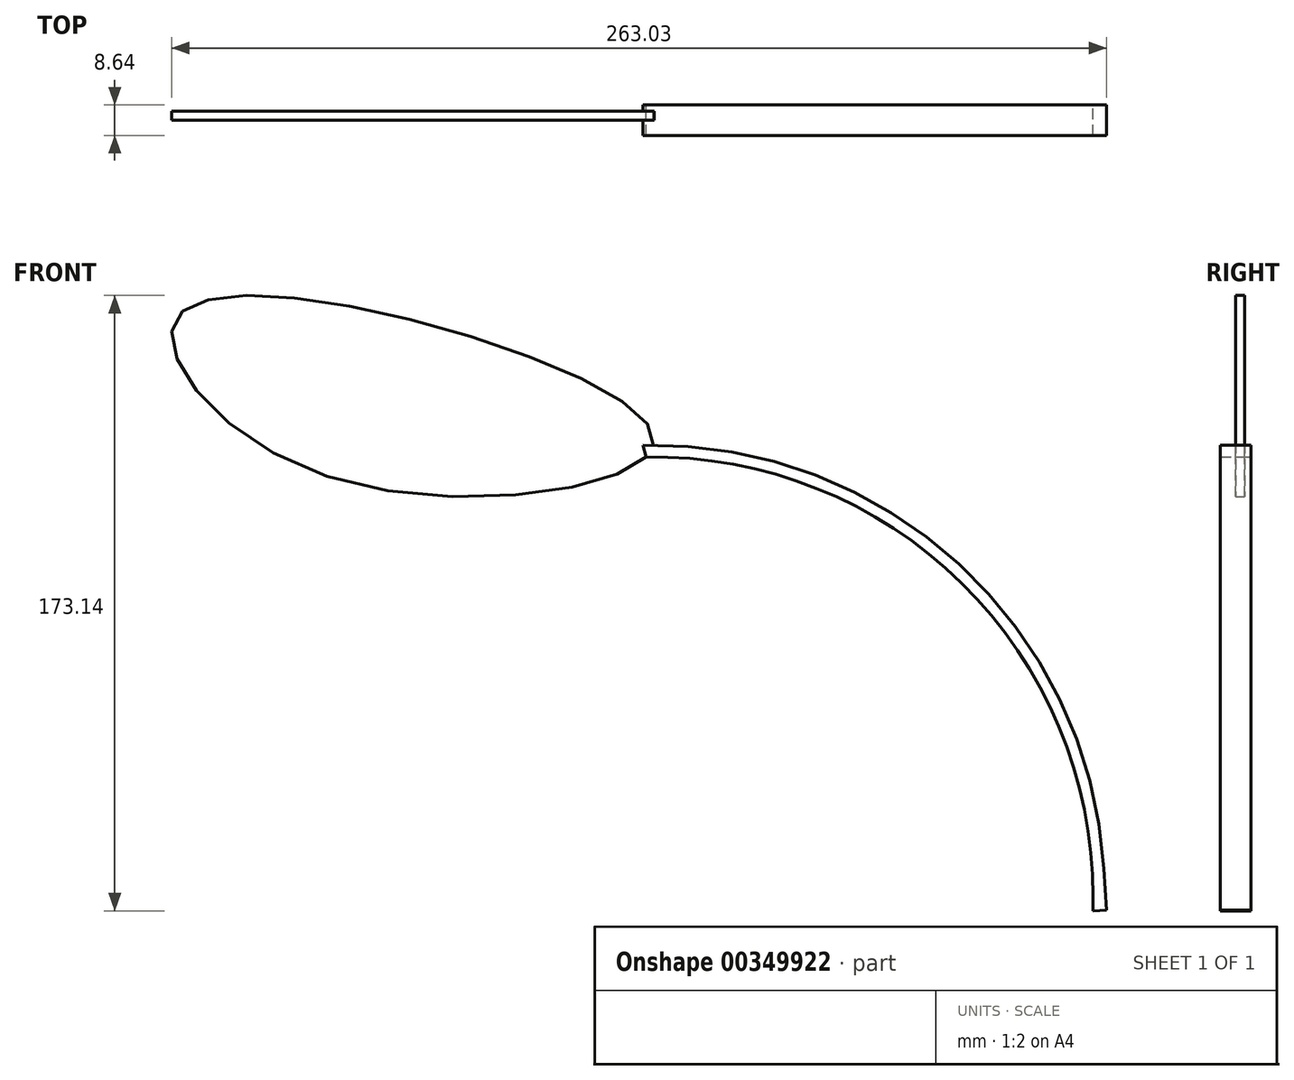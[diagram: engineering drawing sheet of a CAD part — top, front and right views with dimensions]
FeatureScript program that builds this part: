
annotation { "Feature Type Name" : "Feature", "Feature Type Description" : "" }
export const myFeature = defineFeature(function(context is Context, id is Id, definition is map)
    precondition{}
    {
        {
            var Q0;
            Q0=qCreatedBy(makeId("Front.planeOp"),FACE);
            var sketch = newSketch(context, id + "F0", { "sketchPlane" : qUnion([Q0])});
            skFitSpline(sketch, "E0", {"points": [v(0, 0) * mm, v(-70.84, 35.94) * mm, v(-134.9, 34.44) * mm, v(-92.2, -8.57) * mm, v(0, 0) * mm]});
            skSolve(sketch);
        }
        {
            var Q0;
            Q0 = qSketchRegion(id + "F0", true);
            extrude(context, id + "F1", {"entities" : qUnion([Q0]), "depth" : 2.54 * mm, "offsetDistance" : 25.4 * mm});
        }
        {
            var Q0;
            Q0=makeQuery(id+"F1.opExtrude","CAP_FACE",FACE,{"disambiguationData":[OSD([sQuery(id+"F0.wireOp",EDGE,"E0")])],"isStart":false});
            var sketch = newSketch(context, id + "F2", { "sketchPlane" : qUnion([Q0])});
            skArc(sketch, "E1", {"start": v(-2.92, 0) * mm, "mid": v(85.9, -33.42) * mm, "end": v(126.75, -119.07) * mm});
            skArc(sketch, "E2", {"start": v(123.68, -126.97) * mm, "mid": v(86.7, -38.77) * mm, "end": v(-2.1, -3.3) * mm});
            skLineSegment(sketch, "E3", {"start": v(-2.92, 0) * mm, "end": v(-2.1, -3.3) * mm});
            skLineSegment(sketch, "E4", {"start": v(126.75, -119.07) * mm, "end": v(127.48, -130.75) * mm});
            skLineSegment(sketch, "E5", {"start": v(127.48, -130.75) * mm, "end": v(123.68, -130.98) * mm});
            skLineSegment(sketch, "E6", {"start": v(123.68, -130.98) * mm, "end": v(123.68, -126.97) * mm});
            skSolve(sketch);
        }
        {
            var Q0;
            Q0 = qSketchRegion(id + "F2", true);
            extrude(context, id + "F3", {"entities" : qUnion([Q0]), "operationType" : NewBodyOperationType.ADD, "endBound" : BoundingType.SYMMETRIC, "depth" : 8.64 * mm, "offsetDistance" : 25.4 * mm});
        }
    });
